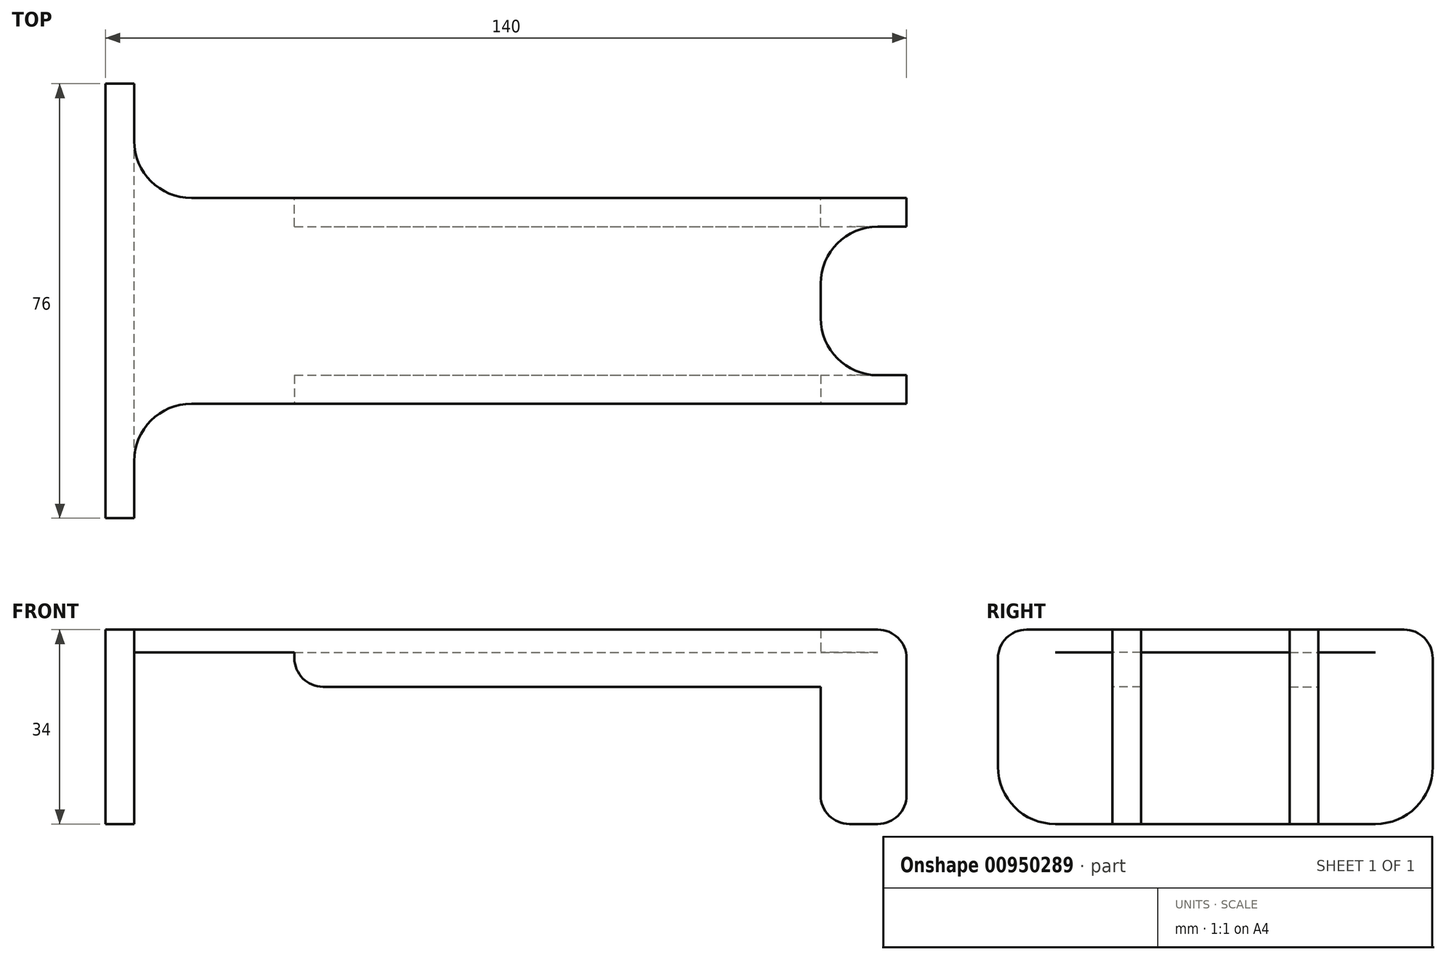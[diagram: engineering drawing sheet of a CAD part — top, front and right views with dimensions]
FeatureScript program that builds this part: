
annotation { "Feature Type Name" : "Feature", "Feature Type Description" : "" }
export const myFeature = defineFeature(function(context is Context, id is Id, definition is map)
    precondition{}
    {
        {
            var Q0;
            Q0=qCreatedBy(makeId("Top.planeOp"),FACE);
            var sketch = newSketch(context, id + "F0", { "sketchPlane" : qUnion([Q0])});
            skLineSegment(sketch, "E0.bottom", {"start": v(28, 9.64) * mm, "end": v(120, 9.64) * mm});
            skLineSegment(sketch, "E0.top", {"start": v(28, -16.36) * mm, "end": v(120, -16.36) * mm});
            skLineSegment(sketch, "E0.left", {"start": v(0, 9.64) * mm, "end": v(0, -16.36) * mm});
            skLineSegment(sketch, "E0.right", {"start": v(120, 9.64) * mm, "end": v(120, -16.36) * mm});
            skLineSegment(sketch, "E1", {"start": v(28, 9.64) * mm, "end": v(28, -16.36) * mm});
            skLineSegment(sketch, "E2", {"start": v(-5, 34.64) * mm, "end": v(-5, -16.36) * mm});
            skLineSegment(sketch, "E3", {"start": v(28, 9.64) * mm, "end": v(28, 14.64) * mm});
            skLineSegment(sketch, "E4", {"start": v(28, 14.64) * mm, "end": v(135, 14.64) * mm});
            skLineSegment(sketch, "E5", {"start": v(135, 14.64) * mm, "end": v(135, 9.64) * mm});
            skLineSegment(sketch, "E6", {"start": v(135, 9.64) * mm, "end": v(120, 9.64) * mm});
            skLineSegment(sketch, "E7", {"start": v(28, -16.36) * mm, "end": v(28, -21.36) * mm});
            skLineSegment(sketch, "E8", {"start": v(28, -21.36) * mm, "end": v(135, -21.36) * mm});
            skLineSegment(sketch, "E9", {"start": v(135, -21.36) * mm, "end": v(135, -16.36) * mm});
            skLineSegment(sketch, "E10", {"start": v(135, -16.36) * mm, "end": v(120, -16.36) * mm});
            skLineSegment(sketch, "E11", {"start": v(120, 9.64) * mm, "end": v(120, 14.64) * mm});
            skLineSegment(sketch, "E12", {"start": v(120, -16.36) * mm, "end": v(120, -21.36) * mm});
            skLineSegment(sketch, "E13", {"start": v(-5, 34.64) * mm, "end": v(0, 34.64) * mm});
            skLineSegment(sketch, "E14", {"start": v(0, 34.64) * mm, "end": v(0, 9.64) * mm});
            skLineSegment(sketch, "E15", {"start": v(-5, -16.36) * mm, "end": v(-5, -41.36) * mm});
            skLineSegment(sketch, "E16", {"start": v(-5, -41.36) * mm, "end": v(0, -41.36) * mm});
            skLineSegment(sketch, "E17", {"start": v(0, -41.36) * mm, "end": v(0, -16.36) * mm});
            skLineSegment(sketch, "E18", {"start": v(28, 14.64) * mm, "end": v(0, 14.64) * mm});
            skPoint(sketch, "E18.endSnap0", {"position": v(0, 22.14) * mm});
            skLineSegment(sketch, "E19", {"start": v(28, -21.36) * mm, "end": v(0, -21.36) * mm});
            skSolve(sketch);
        }
        {
            var Q0;
            {var subQ0=sQuery(id+"F0.wireOp",EDGE,"E0.right");Q0=makeQuery(id+"F0.imprint","IMPRINT",FACE,{"disambiguationData":[TD([[makeQuery(id+"F0.imprint","IMPRINT",EDGE,{"derivedFrom":subQ0}),-1.0]])]});}
            var Q1;
            {var subQ0=sQuery(id+"F0.wireOp",EDGE,"E0.left");Q1=makeQuery(id+"F0.imprint","IMPRINT",FACE,{"disambiguationData":[TD([[makeQuery(id+"F0.imprint","IMPRINT",EDGE,{"derivedFrom":subQ0}),1.0]])]});}
            var Q2;
            {var subQ2=sQuery(id+"F0.wireOp",EDGE,"E3");Q2=makeQuery(id+"F0.imprint","IMPRINT",FACE,{"disambiguationData":[TD([[makeQuery(id+"F0.imprint","IMPRINT",EDGE,{"derivedFrom":subQ2}),-1.0]])]});}
            var Q3;
            {var subQ2=sQuery(id+"F0.wireOp",EDGE,"E7");Q3=makeQuery(id+"F0.imprint","IMPRINT",FACE,{"disambiguationData":[TD([[makeQuery(id+"F0.imprint","IMPRINT",EDGE,{"derivedFrom":subQ2}),1.0]])]});}
            var Q4;
            {var subQ0=sQuery(id+"F0.wireOp",EDGE,"E9");Q4=makeQuery(id+"F0.imprint","IMPRINT",FACE,{"disambiguationData":[TD([[makeQuery(id+"F0.imprint","IMPRINT",EDGE,{"derivedFrom":subQ0}),1.0]])]});}
            var Q5;
            {var subQ0=sQuery(id+"F0.wireOp",EDGE,"E5");Q5=makeQuery(id+"F0.imprint","IMPRINT",FACE,{"disambiguationData":[TD([[makeQuery(id+"F0.imprint","IMPRINT",EDGE,{"derivedFrom":subQ0}),-1.0]])]});}
            var Q6;
            Q6=makeQuery(id+"F0.imprint","IMPRINT",FACE,{"disambiguationData":[TD([[makeQuery(id+"F0.imprint","IMPRINT",EDGE,{"derivedFrom":sQuery(id+"F0.wireOp",EDGE,"E0.left")}),-1.0]])]});
            extrude(context, id + "F1", {"entities" : qUnion([Q0, Q1, Q2, Q3, Q4, Q5, Q6]), "depth" : 4 * mm, "offsetDistance" : 25 * mm});
        }
        {
            var Q0;
            Q0=makeQuery(id+"F0.imprint","IMPRINT",FACE,{"disambiguationData":[TD([[makeQuery(id+"F0.imprint","IMPRINT",EDGE,{"derivedFrom":sQuery(id+"F0.wireOp",EDGE,"E0.left")}),-1.0]])]});
            var Q1;
            {var subQ0=sQuery(id+"F0.wireOp",EDGE,"E9");Q1=makeQuery(id+"F0.imprint","IMPRINT",FACE,{"disambiguationData":[TD([[makeQuery(id+"F0.imprint","IMPRINT",EDGE,{"derivedFrom":subQ0}),1.0]])]});}
            var Q2;
            {var subQ0=sQuery(id+"F0.wireOp",EDGE,"E5");Q2=makeQuery(id+"F0.imprint","IMPRINT",FACE,{"disambiguationData":[TD([[makeQuery(id+"F0.imprint","IMPRINT",EDGE,{"derivedFrom":subQ0}),-1.0]])]});}
            extrude(context, id + "F2", {"entities" : qUnion([Q0, Q1, Q2]), "operationType" : NewBodyOperationType.ADD, "oppositeDirection" : true, "depth" : 30 * mm, "offsetDistance" : 25 * mm});
        }
        {
            var Q0;
            {var subQ2=sQuery(id+"F0.wireOp",EDGE,"E7");Q0=makeQuery(id+"F0.imprint","IMPRINT",FACE,{"disambiguationData":[TD([[makeQuery(id+"F0.imprint","IMPRINT",EDGE,{"derivedFrom":subQ2}),1.0]])]});}
            var Q1;
            {var subQ2=sQuery(id+"F0.wireOp",EDGE,"E3");Q1=makeQuery(id+"F0.imprint","IMPRINT",FACE,{"disambiguationData":[TD([[makeQuery(id+"F0.imprint","IMPRINT",EDGE,{"derivedFrom":subQ2}),-1.0]])]});}
            extrude(context, id + "F3", {"entities" : qUnion([Q0, Q1]), "operationType" : NewBodyOperationType.ADD, "oppositeDirection" : true, "depth" : 6 * mm, "offsetDistance" : 25 * mm});
        }
        {
            var Q0;
            Q0=makeQuery(id+"F1.opExtrude","SWEPT_EDGE",EDGE,{"disambiguationData":[OSD([sQuery(id+"F0.wireOp",EDGE,"E17"),sQuery(id+"F0.wireOp",EDGE,"E19")])]});
            var Q1;
            Q1=makeQuery(id+"F1.opExtrude","SWEPT_EDGE",EDGE,{"disambiguationData":[OSD([sQuery(id+"F0.wireOp",EDGE,"E14"),sQuery(id+"F0.wireOp",EDGE,"E18")])]});
            var Q2;
            Q2=makeQuery(id+"F1.opExtrude","SWEPT_EDGE",EDGE,{"disambiguationData":[OSD([sQuery(id+"F0.wireOp",EDGE,"E0.bottom"),sQuery(id+"F0.wireOp",EDGE,"E0.right"),sQuery(id+"F0.wireOp",EDGE,"E6"),sQuery(id+"F0.wireOp",EDGE,"E11")])]});
            var Q3;
            Q3=makeQuery(id+"F1.opExtrude","SWEPT_EDGE",EDGE,{"disambiguationData":[OSD([sQuery(id+"F0.wireOp",EDGE,"E0.top"),sQuery(id+"F0.wireOp",EDGE,"E0.right"),sQuery(id+"F0.wireOp",EDGE,"E10"),sQuery(id+"F0.wireOp",EDGE,"E12")])]});
            var Q4;
            Q4=makeQuery(id+"F2.opExtrude","CAP_EDGE",EDGE,{"disambiguationData":[OSD([sQuery(id+"F0.wireOp",EDGE,"E16")])],"isStart":false});
            var Q5;
            Q5=makeQuery(id+"F2.opExtrude","CAP_EDGE",EDGE,{"disambiguationData":[OSD([sQuery(id+"F0.wireOp",EDGE,"E13")])],"isStart":false});
            fillet(context, id + "F4", {"entities" : qUnion([Q0, Q1, Q2, Q3, Q4, Q5]), "radius" : 10 * mm, "tangentPropagation" : true, "allowEdgeOverflow" : false});
        }
        {
            var Q0;
            Q0=makeQuery(id+"F2.opExtrude","CAP_EDGE",EDGE,{"disambiguationData":[OSD([sQuery(id+"F0.wireOp",EDGE,"E5")])],"isStart":false});
            var Q1;
            Q1=makeQuery(id+"F2.opExtrude","CAP_EDGE",EDGE,{"disambiguationData":[OSD([sQuery(id+"F0.wireOp",EDGE,"E11")])],"isStart":false});
            var Q2;
            Q2=makeQuery(id+"F2.opExtrude","CAP_EDGE",EDGE,{"disambiguationData":[OSD([sQuery(id+"F0.wireOp",EDGE,"E9")])],"isStart":false});
            var Q3;
            Q3=makeQuery(id+"F2.opExtrude","CAP_EDGE",EDGE,{"disambiguationData":[OSD([sQuery(id+"F0.wireOp",EDGE,"E12")])],"isStart":false});
            var Q4;
            Q4=makeQuery(id+"F1.opExtrude","CAP_EDGE",EDGE,{"disambiguationData":[OSD([sQuery(id+"F0.wireOp",EDGE,"E5")])],"isStart":false});
            var Q5;
            Q5=makeQuery(id+"F1.opExtrude","CAP_EDGE",EDGE,{"disambiguationData":[OSD([sQuery(id+"F0.wireOp",EDGE,"E9")])],"isStart":false});
            var Q6;
            Q6=makeQuery(id+"F1.opExtrude","CAP_EDGE",EDGE,{"disambiguationData":[OSD([sQuery(id+"F0.wireOp",EDGE,"E16")])],"isStart":false});
            var Q7;
            Q7=makeQuery(id+"F1.opExtrude","CAP_EDGE",EDGE,{"disambiguationData":[OSD([sQuery(id+"F0.wireOp",EDGE,"E13")])],"isStart":false});
            var Q8;
            Q8=makeQuery(id+"F3.opExtrude","CAP_EDGE",EDGE,{"disambiguationData":[OSD([sQuery(id+"F0.wireOp",EDGE,"E3")])],"isStart":false});
            var Q9;
            Q9=makeQuery(id+"F3.opExtrude","CAP_EDGE",EDGE,{"disambiguationData":[OSD([sQuery(id+"F0.wireOp",EDGE,"E7")])],"isStart":false});
            var Q10;
            Q10=makeQuery(id+"F2.opExtrude","CAP_EDGE",EDGE,{"disambiguationData":[OSD([sQuery(id+"F0.wireOp",EDGE,"E0.left"),sQuery(id+"F0.wireOp",EDGE,"E14"),sQuery(id+"F0.wireOp",EDGE,"E17")])],"isStart":true});
            fillet(context, id + "F5", {"entities" : qUnion([Q0, Q1, Q2, Q3, Q4, Q5, Q6, Q7, Q8, Q9, Q10]), "radius" : 5 * mm, "tangentPropagation" : true, "allowEdgeOverflow" : false});
        }
    });
